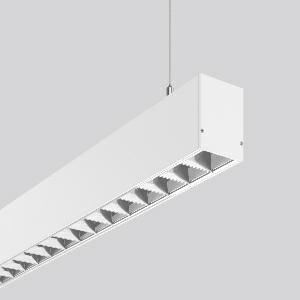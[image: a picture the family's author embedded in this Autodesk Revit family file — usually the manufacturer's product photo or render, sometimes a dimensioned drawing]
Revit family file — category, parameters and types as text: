
# Revit family: less_is_more_50_312336_002_1_d1b4
name_source: partatom
category: Lighting Fixtures
units: mm (PartAtom-declared; Revit-internal decimal feet)

## family parameters
Cut with Voids When Loaded = No
Host = Face
Light Source = No
Part Type = Normal
Room Calculation Point = No
Round Connector Dimension = Use Diameter
Shared = No

## types (1)
- LESS IS MORE 50 (1 x LED Modul 840, 3550 lm, 4000)
    Apparent Load = 28 VA
    CIE Flux Codes = 95 100 100 100 100
    Color Rendering = 80
    Color Temperature = 4000
    Default Elevation = 1800 mm
    Description = Series: LESS IS MORE 50
Linear pendant luminaire for aesthetically sophisticated lighting. Housing: extruded aluminium profile, powder-coated. End cap aluminium powder-coated. Canopy made of aluminium, powder-coated. Alea optical system: Reflector structure (ABS, Aluminium-coated, highly polished) with integrated diffuser made of non-yellowing plastic (PMMA) opal for glare-free light at the workstation (screen-compliant according to EN 12464-1). Direct light emission. Suitable for pendant. 2-point steel cable suspension freely positionable and infinitely height-adjustable. Special lengths available on request. LED unit with integrated converter interchangeable and removable. Suitable for through-wiring. With sensors or as a safety luminaire on request. 
Colour: traffic white, matt (RAL 9016)
Length: 1127 mm
Width: 57 mm
Height: 75 mm
Suspension length: 2000 mm
Lamp: LED
Socket: without socket
Colour temperature: 4000K
Colour rendering index (CRI): 80
System power: 28 W
Rated luminous flux: 3550 lm
Luminous efficiency: 127 lm/W
Control gear: Regulated power supply
Protection class: I
Type of protection: IP 20
    Height = 75 mm
    Lamp = 1 x LED Modul 840
    Lamp Light Flux = 3550 lm
    Lamp count = 1
    Length = 1127 mm
    Lifetime = 50000 h
    Luminous efficacy = 127 lm/W
    Manufacturer = RZB
    ModVariant = No
    Model = 312336.002.1
    Mounting Place = Ceiling
    Mounting Type = Pendant
    Number of Poles = 1
    OnlyDefault = Yes
    Power Factor = 1
    Product Name = LESS IS MORE 50
    Product group = Pendant LED linear luminaires
    ProductGroupID = 907
    Protection Class = Protection class I
    Protection Degree = IP 20
    RLX_Detail_Level = 1
    RLX_Emergency_Light_Flux = 0 lm
    RLX_Emergency_Type = 0
    RLX_Emergency_Type_DB = No
    RlxData = <blob elided: 33193 chars, md5=0f4f2f51>
    Socket = socket
    Standby Power = 0 W
    System Light Flux = 3550 lm
    System Power = 28 W
    Type Comments = Product without accessories
    Type Image = 312342.002.jpg
    URL = http://relux.com
    VarID = ---
    Voltage = 230 V
    Voltage Range = 220-240 V
    Weight = 0.00 kg
    Width = 57 mm

## geometry (parser evidence)
native form markers: Blend x4, Sweep x10
no freeform markers — native parametric forms only
